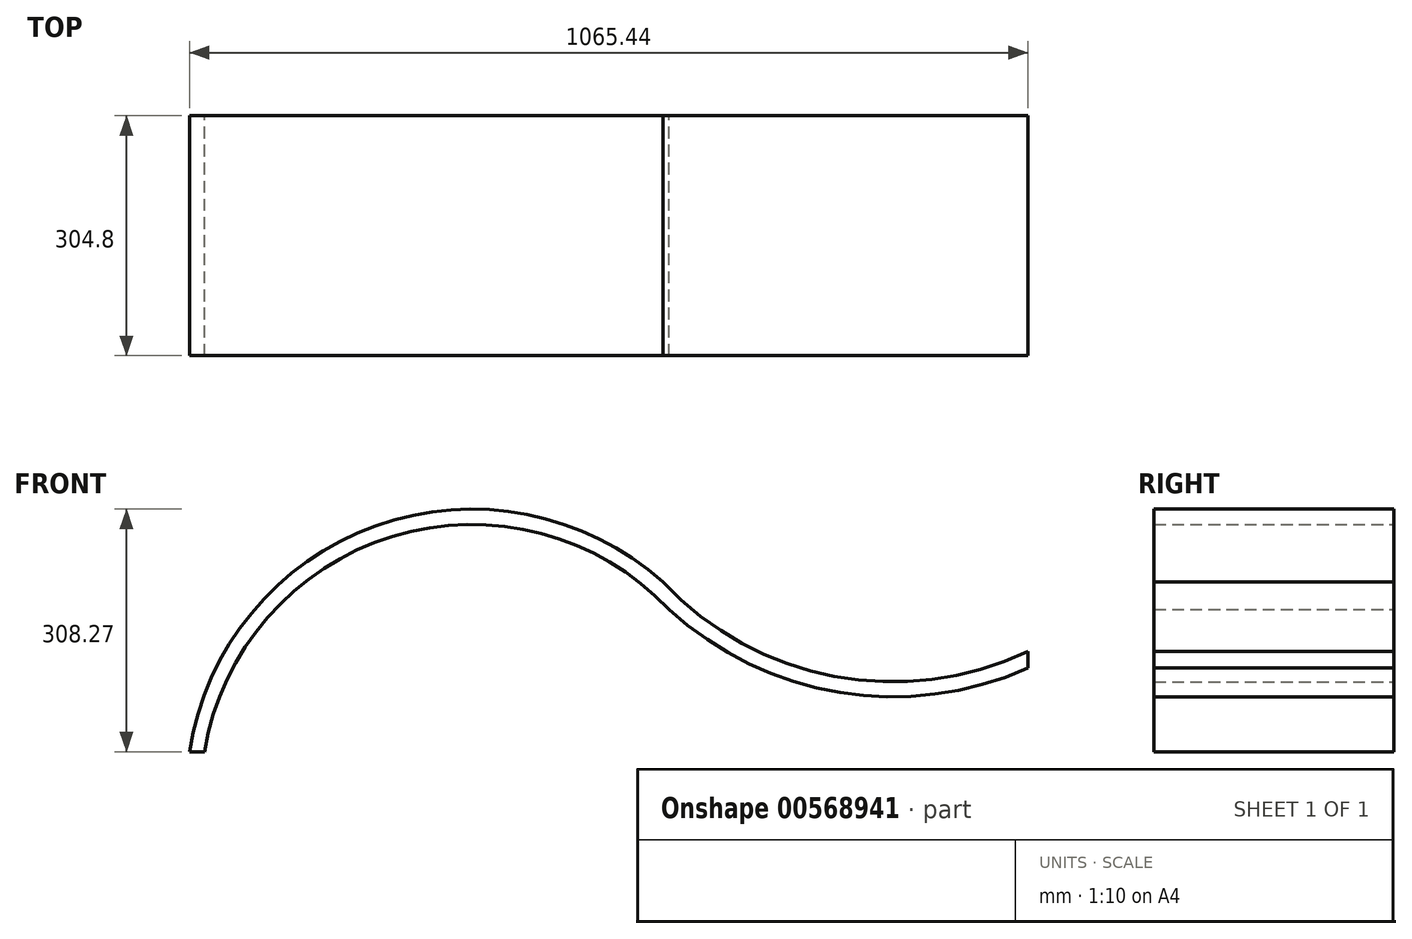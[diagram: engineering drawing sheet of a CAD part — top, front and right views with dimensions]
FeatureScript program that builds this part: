
annotation { "Feature Type Name" : "Feature", "Feature Type Description" : "" }
export const myFeature = defineFeature(function(context is Context, id is Id, definition is map)
    precondition{}
    {
        {
            var Q0;
            Q0=qCreatedBy(makeId("Front.planeOp"),FACE);
            var sketch = newSketch(context, id + "F0", { "sketchPlane" : qUnion([Q0])});
            skLineSegment(sketch, "E0", {"start": v(344.3, -39.5) * mm, "end": v(-722.5, -39.5) * mm});
            skPoint(sketch, "E1", {"position": v(-363.46, -94.44) * mm});
            skArc(sketch, "E2", {"start": v(-722.5, -39.5) * mm, "mid": v(-485.97, 247.5) * mm, "end": v(-121, 176) * mm});
            skArc(sketch, "E3", {"start": v(-121, 176) * mm, "mid": v(96.5, 56.54) * mm, "end": v(342.68, 87.82) * mm});
            skLineSegment(sketch, "E4", {"start": v(342.68, 87.82) * mm, "end": v(344.3, -39.5) * mm});
            skLineSegment(sketch, "E5", {"start": v(-121, 176) * mm, "end": v(-121, -39.5) * mm});
            skLineSegment(sketch, "E6", {"start": v(-121, -39.5) * mm, "end": v(344.3, -39.5) * mm});
            skArc(sketch, "E7", {"start": v(-23.7, -39.5) * mm, "mid": v(-363.46, 249.35) * mm, "end": v(-703.22, -39.5) * mm});
            skArc(sketch, "E8", {"start": v(-248.88, 450.8) * mm, "mid": v(171.49, 30.42) * mm, "end": v(591.86, 450.8) * mm});
            skSolve(sketch);
        }
        {
            var Q0;
            {var subQ0=sQuery(id+"F0.wireOp",EDGE,"E2");var subQ1=sQuery(id+"F0.wireOp",EDGE,"E0");var subQ2=makeQuery(id+"F0.imprint","INTERSECT",VERTEX,{"derivedFrom":[subQ1,subQ0]});Q0=makeQuery(id+"F0.imprint","IMPRINT",FACE,{"disambiguationData":[TD([[makeQuery(id+"F0.imprint","IMPRINT",EDGE,{"disambiguationData":[TD([[subQ2,1.0]])],"derivedFrom":subQ1}),-1.0]])]});}
            var Q1;
            {var subQ0=sQuery(id+"F0.wireOp",EDGE,"E5");var subQ5=sQuery(id+"F0.wireOp",EDGE,"E7");var subQ6=makeQuery(id+"F0.imprint","INTERSECT",VERTEX,{"derivedFrom":[subQ0,subQ5]});Q1=makeQuery(id+"F0.imprint","IMPRINT",FACE,{"disambiguationData":[TD([[makeQuery(id+"F0.imprint","IMPRINT",EDGE,{"disambiguationData":[TD([[subQ6,-1.0]])],"derivedFrom":subQ5}),-1.0]])]});}
            var Q2;
            {var subQ5=sQuery(id+"F0.wireOp",EDGE,"E3");Q2=makeQuery(id+"F0.imprint","IMPRINT",FACE,{"disambiguationData":[TD([[makeQuery(id+"F0.imprint","IMPRINT",EDGE,{"derivedFrom":subQ5}),-1.0]])]});}
            extrude(context, id + "F1", {"entities" : qUnion([Q0, Q1, Q2]), "depth" : 304.8 * mm, "offsetDistance" : 25.4 * mm});
        }
    });
